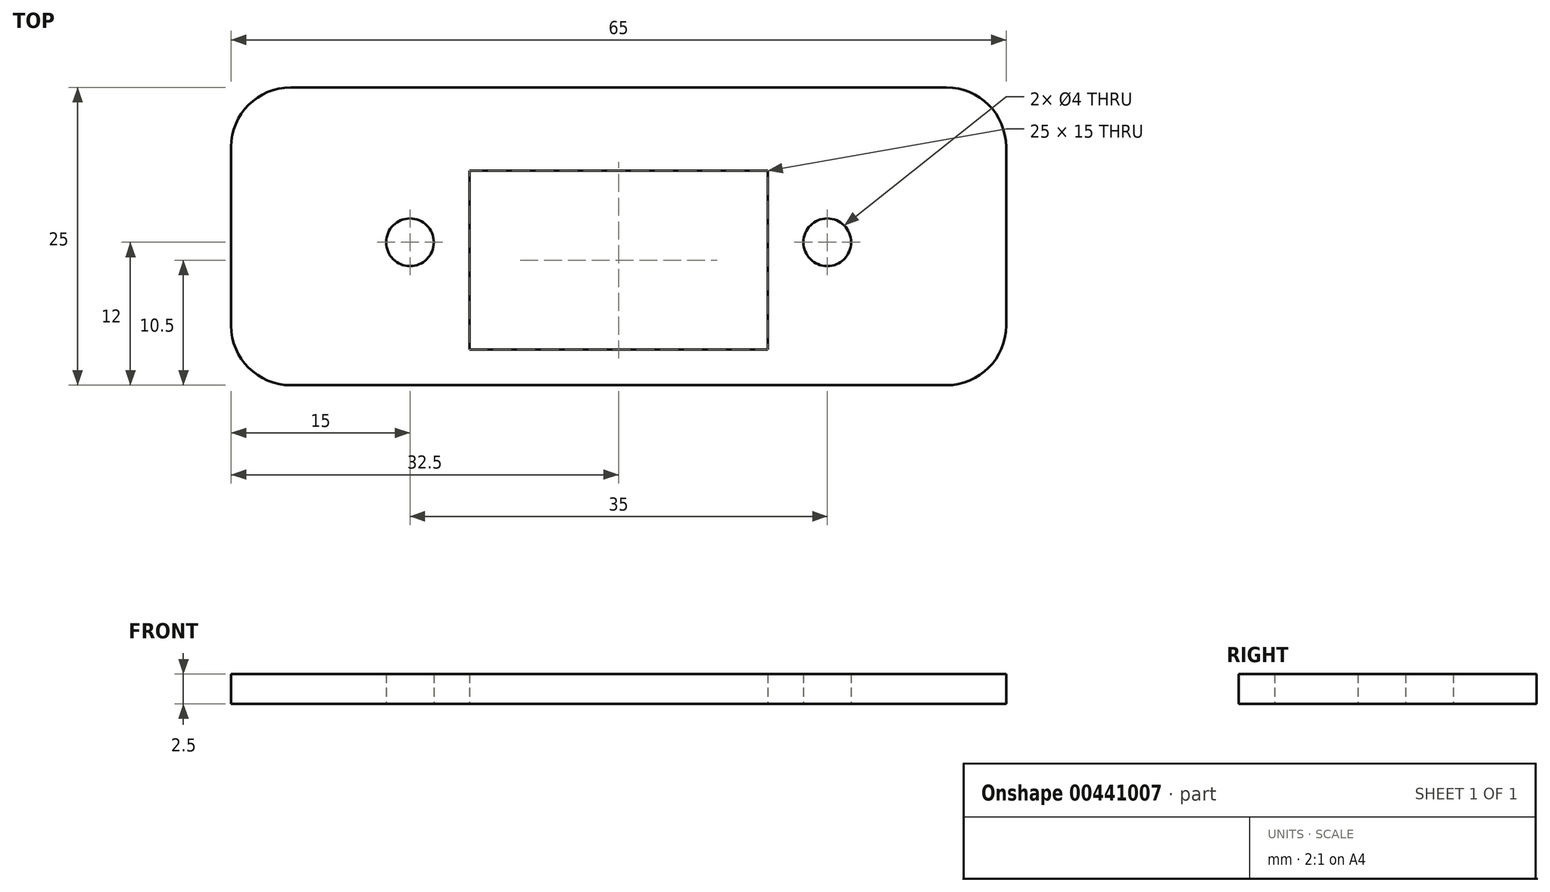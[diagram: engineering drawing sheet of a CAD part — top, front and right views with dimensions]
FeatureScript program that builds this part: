
annotation { "Feature Type Name" : "Feature", "Feature Type Description" : "" }
export const myFeature = defineFeature(function(context is Context, id is Id, definition is map)
    precondition{}
    {
        {
            var Q0;
            Q0=qCreatedBy(makeId("Top.planeOp"),FACE);
            var sketch = newSketch(context, id + "F0", { "sketchPlane" : qUnion([Q0])});
            skLineSegment(sketch, "E0.bottom", {"start": v(-32.5, 13) * mm, "end": v(32.5, 13) * mm});
            skLineSegment(sketch, "E0.top", {"start": v(-32.5, -12) * mm, "end": v(32.5, -12) * mm});
            skLineSegment(sketch, "E0.left", {"start": v(-32.5, 13) * mm, "end": v(-32.5, -12) * mm});
            skLineSegment(sketch, "E0.right", {"start": v(32.5, 13) * mm, "end": v(32.5, -12) * mm});
            skPoint(sketch, "E1.middle", {"position": v(0, 0) * mm});
            skCircle(sketch, "E2", {"center": v(-17.5, 0) * mm, "radius": 2 * mm});
            skCircle(sketch, "E3.MirrorC", {"center": v(17.5, 0) * mm, "radius": 2 * mm});
            skLineSegment(sketch, "E4.bottom", {"start": v(-12.5, 6) * mm, "end": v(12.5, 6) * mm});
            skLineSegment(sketch, "E4.top", {"start": v(-12.5, -9) * mm, "end": v(12.5, -9) * mm});
            skLineSegment(sketch, "E4.left", {"start": v(-12.5, 6) * mm, "end": v(-12.5, -9) * mm});
            skLineSegment(sketch, "E4.right", {"start": v(12.5, 6) * mm, "end": v(12.5, -9) * mm});
            skSolve(sketch);
        }
        {
            var Q0;
            Q0 = qSketchRegion(id + "F0", true);
            extrude(context, id + "F1", {"entities" : qUnion([Q0]), "depth" : 2.5 * mm});
        }
        {
            var Q0;
            Q0=makeQuery(id+"F1.opExtrude","SWEPT_EDGE",EDGE,{"disambiguationData":[OSD([sQuery(id+"F0.wireOp",EDGE,"E0.bottom"),sQuery(id+"F0.wireOp",EDGE,"E0.right")])]});
            fillet(context, id + "F2", {"entities" : qUnion([Q0]), "radius" : 5 * mm, "tangentPropagation" : true, "allowEdgeOverflow" : false});
        }
        {
            var Q0;
            Q0=makeQuery(id+"F1.opExtrude","SWEPT_EDGE",EDGE,{"disambiguationData":[OSD([sQuery(id+"F0.wireOp",EDGE,"E0.top"),sQuery(id+"F0.wireOp",EDGE,"E0.right")])]});
            var Q1;
            Q1=makeQuery(id+"F1.opExtrude","SWEPT_EDGE",EDGE,{"disambiguationData":[OSD([sQuery(id+"F0.wireOp",EDGE,"E0.top"),sQuery(id+"F0.wireOp",EDGE,"E0.left")])]});
            var Q2;
            Q2=makeQuery(id+"F1.opExtrude","SWEPT_EDGE",EDGE,{"disambiguationData":[OSD([sQuery(id+"F0.wireOp",EDGE,"E0.bottom"),sQuery(id+"F0.wireOp",EDGE,"E0.left")])]});
            fillet(context, id + "F3", {"entities" : qUnion([Q0, Q1, Q2]), "radius" : 5 * mm, "tangentPropagation" : true, "allowEdgeOverflow" : false});
        }
    });
